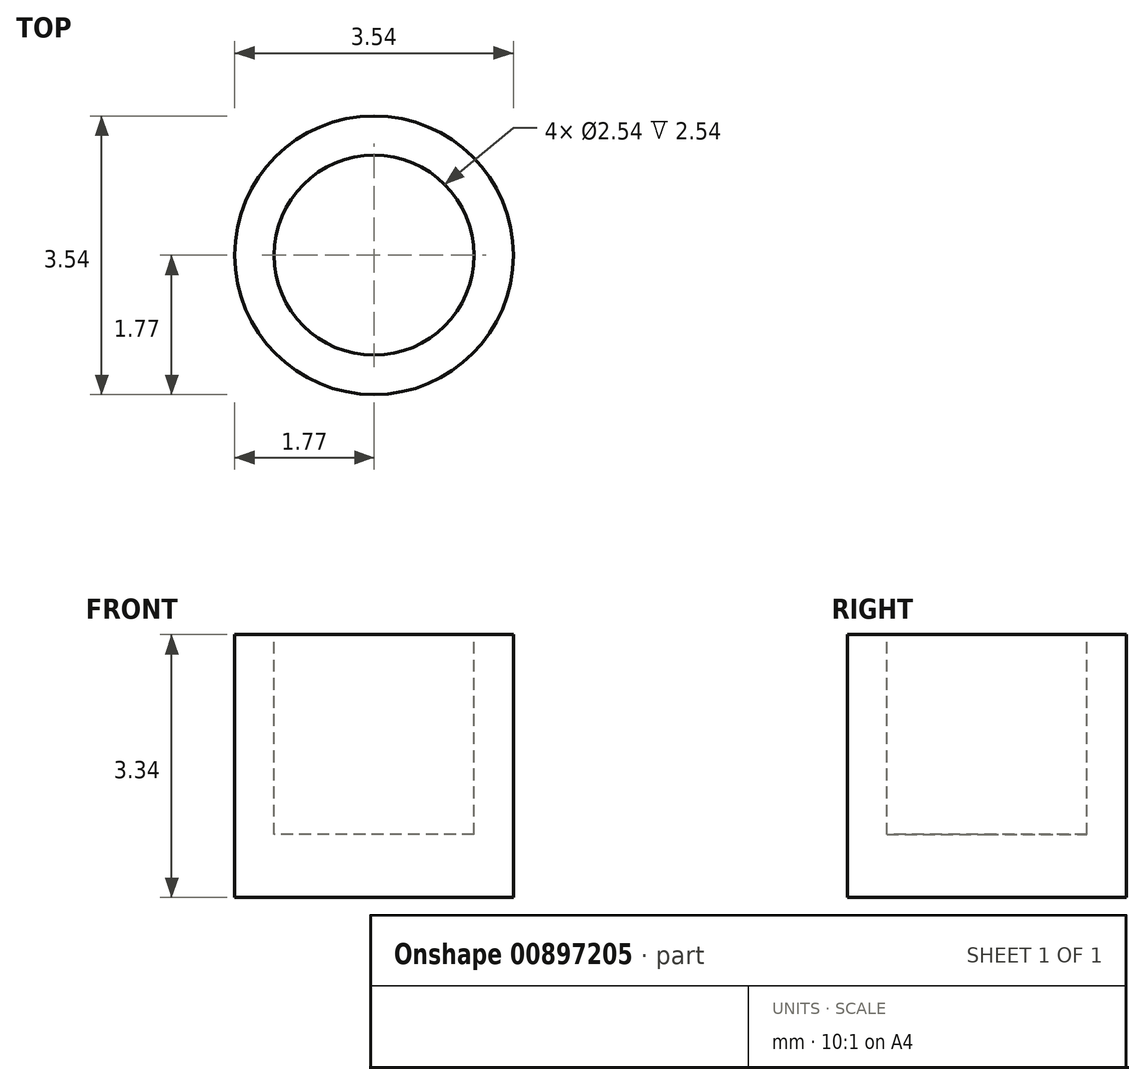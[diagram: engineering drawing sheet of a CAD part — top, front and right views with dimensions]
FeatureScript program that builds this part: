
annotation { "Feature Type Name" : "Feature", "Feature Type Description" : "" }
export const myFeature = defineFeature(function(context is Context, id is Id, definition is map)
    precondition{}
    {
        {
            var Q0;
            Q0=qCreatedBy(makeId("Top.planeOp"),FACE);
            var sketch = newSketch(context, id + "F0", { "sketchPlane" : qUnion([Q0])});
            skCircle(sketch, "E0", {"center": v(0, 0) * mm, "radius": 1.77 * mm});
            skSolve(sketch);
        }
        {
            var Q0;
            Q0 = qSketchRegion(id + "F0", true);
            extrude(context, id + "F1", {"entities" : qUnion([Q0]), "depth" : 2.54 * mm + .8 * mm, "offsetDistance" : 25.4 * mm});
        }
        {
            var Q0;
            Q0=makeQuery(id+"F1.opExtrude","CAP_FACE",FACE,{"disambiguationData":[OSD([sQuery(id+"F0.wireOp",EDGE,"E0")])],"isStart":false});
            var sketch = newSketch(context, id + "F2", { "sketchPlane" : qUnion([Q0])});
            skPoint(sketch, "E1.0", {"position": v(0, 0) * mm});
            skCircle(sketch, "E2", {"center": v(0, 0) * mm, "radius": 1.27 * mm});
            skSolve(sketch);
        }
        {
            var Q0;
            Q0=makeQuery(id+"F2.imprint","IMPRINT",FACE,{"disambiguationData":[TD([[makeQuery(id+"F2.imprint","IMPRINT",EDGE,{"derivedFrom":sQuery(id+"F2.wireOp",EDGE,"E2")}),1.0]])]});
            extrude(context, id + "F3", {"entities" : qUnion([Q0]), "operationType" : NewBodyOperationType.REMOVE, "oppositeDirection" : true, "depth" : 2.54 * mm, "offsetDistance" : 25.4 * mm});
        }
    });
